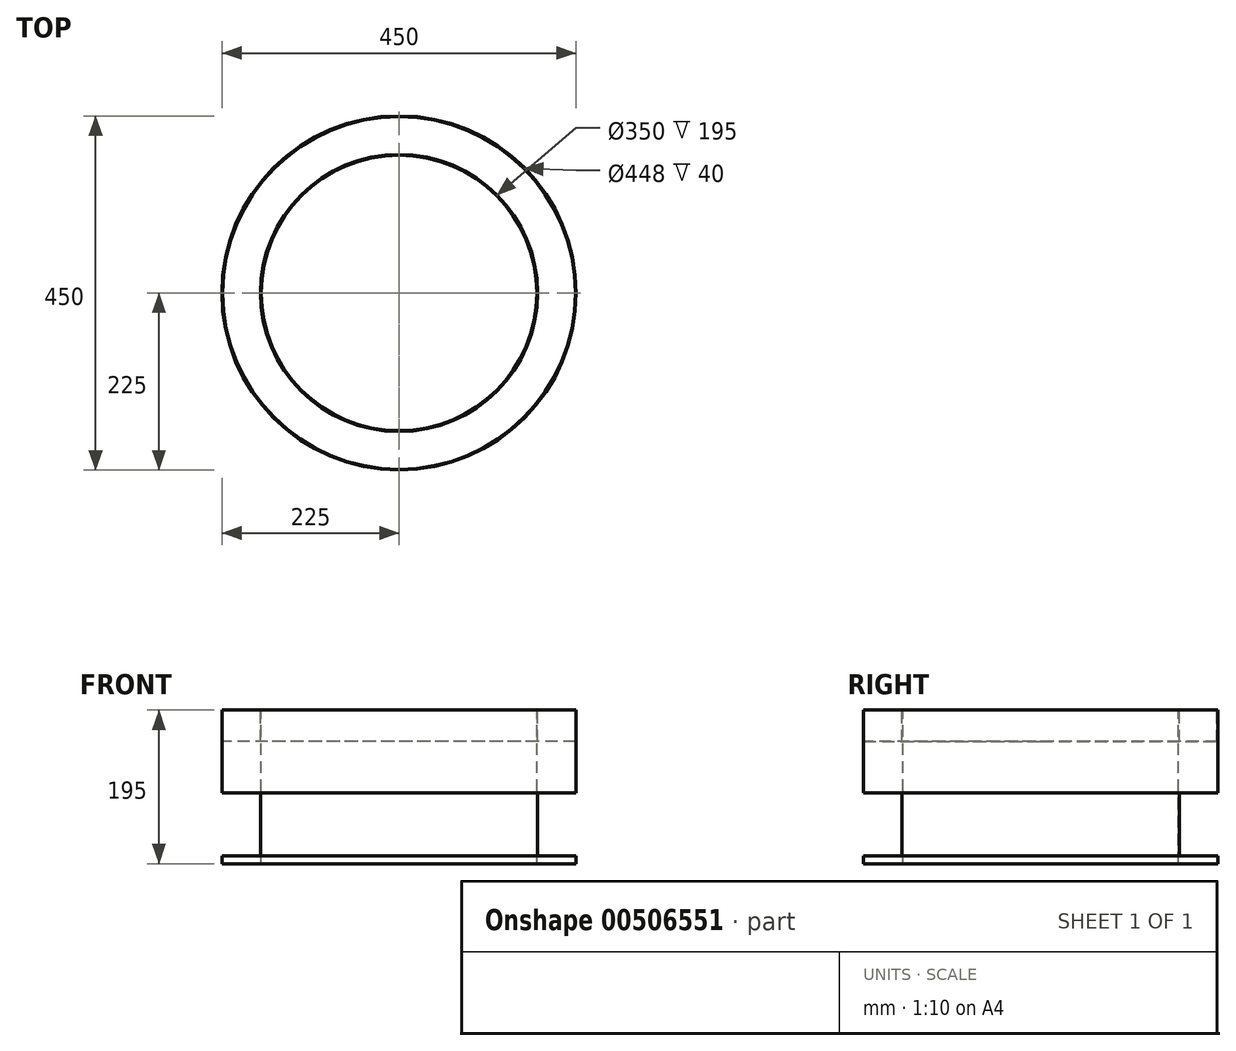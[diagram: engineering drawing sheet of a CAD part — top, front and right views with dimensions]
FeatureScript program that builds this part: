
annotation { "Feature Type Name" : "Feature", "Feature Type Description" : "" }
export const myFeature = defineFeature(function(context is Context, id is Id, definition is map)
    precondition{}
    {
        {
            var Q0;
            Q0=qCreatedBy(makeId("Front.planeOp"),FACE);
            var sketch = newSketch(context, id + "F0", { "sketchPlane" : qUnion([Q0])});
            skLineSegment(sketch, "E0", {"start": v(0, 710.75) * mm, "end": v(0, -704.58) * mm, "construction": true});
            skLineSegment(sketch, "E1", {"start": v(-175, 300.65) * mm, "end": v(-175, 495.65) * mm});
            skLineSegment(sketch, "E2", {"start": v(-175, 495.65) * mm, "end": v(-176, 495.65) * mm});
            skLineSegment(sketch, "E3", {"start": v(-224, 495.65) * mm, "end": v(-225, 495.65) * mm});
            skLineSegment(sketch, "E4", {"start": v(-225, 495.65) * mm, "end": v(-225, 390.65) * mm});
            skLineSegment(sketch, "E5", {"start": v(-225, 390.65) * mm, "end": v(-176, 390.65) * mm});
            skLineSegment(sketch, "E6", {"start": v(-176, 390.65) * mm, "end": v(-176, 310.65) * mm});
            skLineSegment(sketch, "E7", {"start": v(-176, 310.65) * mm, "end": v(-225, 310.65) * mm});
            skLineSegment(sketch, "E8", {"start": v(-225, 310.65) * mm, "end": v(-225, 300.65) * mm});
            skLineSegment(sketch, "E9", {"start": v(-225, 300.65) * mm, "end": v(-175, 300.65) * mm});
            skLineSegment(sketch, "E10", {"start": v(-224, 495.65) * mm, "end": v(-224, 455.65) * mm});
            skLineSegment(sketch, "E11", {"start": v(-224, 455.65) * mm, "end": v(-176, 455.65) * mm});
            skLineSegment(sketch, "E12", {"start": v(-176, 455.65) * mm, "end": v(-176, 495.65) * mm});
            skSolve(sketch);
        }
        {
            var Q0;
            Q0=qSketchRegion(id+"F0",true);
            var Q1;
            Q1=sQuery(id+"F0.wireOp",EDGE,"E0");
            revolve(context, id + "F1", {"entities" : qUnion([Q0]), "axis" : qUnion([Q1]), "revolveType" : RevolveType.FULL});
        }
    });
